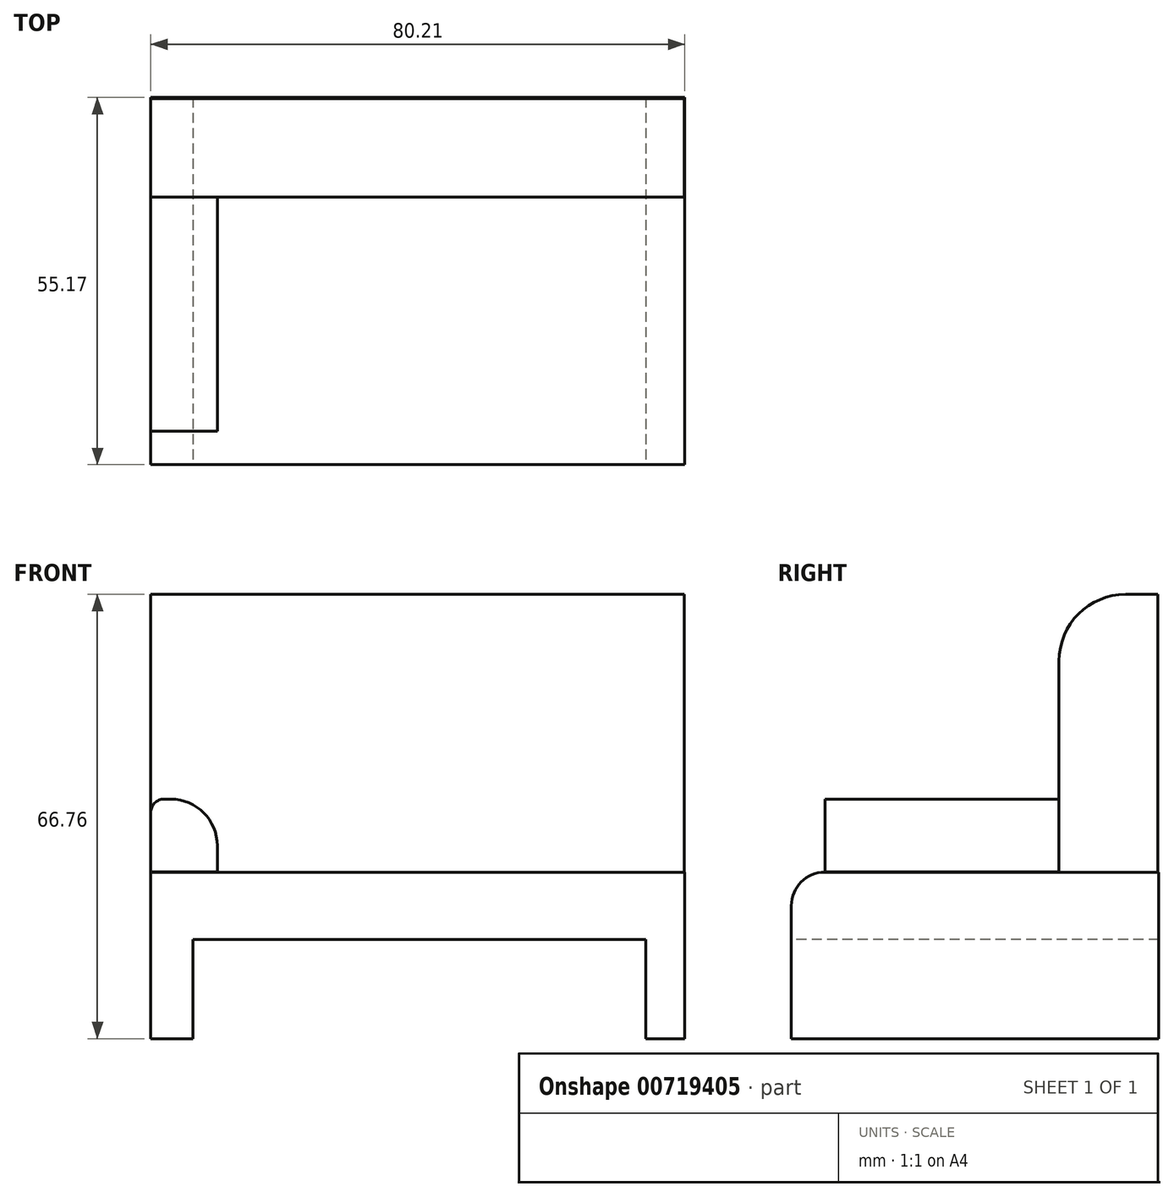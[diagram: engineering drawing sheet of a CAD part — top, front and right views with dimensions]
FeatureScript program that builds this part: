
annotation { "Feature Type Name" : "Feature", "Feature Type Description" : "" }
export const myFeature = defineFeature(function(context is Context, id is Id, definition is map)
    precondition{}
    {
        {
            var Q0;
            Q0=qCreatedBy(makeId("Top.planeOp"),FACE);
            var sketch = newSketch(context, id + "F0", { "sketchPlane" : qUnion([Q0])});
            skLineSegment(sketch, "E0.bottom", {"start": v(0, 0) * mm, "end": v(80.21, 0) * mm});
            skLineSegment(sketch, "E0.top", {"start": v(0, 55.17) * mm, "end": v(80.21, 55.17) * mm});
            skLineSegment(sketch, "E0.left", {"start": v(0, 0) * mm, "end": v(0, 55.17) * mm});
            skLineSegment(sketch, "E0.right", {"start": v(80.21, 0) * mm, "end": v(80.21, 55.17) * mm});
            skSolve(sketch);
        }
        {
            var Q0;
            Q0=makeQuery(id+"F0.imprint","IMPRINT",FACE,{"disambiguationData":[TD([[makeQuery(id+"F0.imprint","IMPRINT",EDGE,{"derivedFrom":sQuery(id+"F0.wireOp",EDGE,"E0.bottom")}),1.0]])]});
            extrude(context, id + "F1", {"entities" : qUnion([Q0]), "depth" : 25 * mm, "offsetDistance" : 25 * mm});
        }
        {
            var Q0;
            Q0=qCreatedBy(makeId("Front.planeOp"),FACE);
            cPlane(context, id + "F2", {"entities" : qUnion([Q0]), "cplaneType" : CPlaneType.OFFSET, "offset" : 55 * mm, "oppositeDirection" : true, "width" : 150 * mm, "height" : 150 * mm});
        }
        {
            var Q0;
            Q0=qCreatedBy(id+"F2.planeOp",FACE);
            var sketch = newSketch(context, id + "F3", { "sketchPlane" : qUnion([Q0])});
            skLineSegment(sketch, "E1.bottom", {"start": v(80.1, 0) * mm, "end": v(0, 0) * mm});
            skLineSegment(sketch, "E1.top", {"start": v(80.1, 66.76) * mm, "end": v(0, 66.76) * mm});
            skLineSegment(sketch, "E1.left", {"start": v(80.1, 0) * mm, "end": v(80.1, 66.76) * mm});
            skLineSegment(sketch, "E1.right", {"start": v(0, 0) * mm, "end": v(0, 66.76) * mm});
            skSolve(sketch);
        }
        {
            var Q0;
            Q0 = qSketchRegion(id + "F3", true);
            extrude(context, id + "F4", {"entities" : qUnion([Q0]), "operationType" : NewBodyOperationType.ADD, "depth" : 14.8 * mm, "offsetDistance" : 25 * mm});
        }
        {
            var Q0;
            Q0=qCreatedBy(makeId("Right.planeOp"),FACE);
            cPlane(context, id + "F5", {"entities" : qUnion([Q0]), "cplaneType" : CPlaneType.OFFSET, "offset" : 40 * mm, "width" : 150 * mm, "height" : 150 * mm});
        }
        {
            var Q0;
            Q0=qCreatedBy(makeId("Front.planeOp"),FACE);
            var sketch = newSketch(context, id + "F6", { "sketchPlane" : qUnion([Q0])});
            skLineSegment(sketch, "E2.bottom", {"start": v(6.36, 0) * mm, "end": v(74.33, 0) * mm});
            skLineSegment(sketch, "E2.top", {"start": v(6.36, 14.87) * mm, "end": v(74.33, 14.87) * mm});
            skLineSegment(sketch, "E2.left", {"start": v(6.36, 0) * mm, "end": v(6.36, 14.87) * mm});
            skLineSegment(sketch, "E2.right", {"start": v(74.33, 0) * mm, "end": v(74.33, 14.87) * mm});
            skSolve(sketch);
        }
        {
            var Q0;
            Q0 = qSketchRegion(id + "F6", true);
            extrude(context, id + "F7", {"entities" : qUnion([Q0]), "operationType" : NewBodyOperationType.REMOVE, "oppositeDirection" : true, "depth" : 99 * mm, "offsetDistance" : 25 * mm});
        }
        {
            var Q0;
            Q0=makeQuery(id+"F1.opExtrude","CAP_EDGE",EDGE,{"disambiguationData":[OSD([sQuery(id+"F0.wireOp",EDGE,"E0.bottom")])],"isStart":false});
            fillet(context, id + "F8", {"entities" : qUnion([Q0]), "radius" : 5 * mm, "tangentPropagation" : true, "allowEdgeOverflow" : false});
        }
        {
            var Q0;
            Q0=qCreatedBy(makeId("Right.planeOp"),FACE);
            var sketch = newSketch(context, id + "F9", { "sketchPlane" : qUnion([Q0])});
            skLineSegment(sketch, "E3.bottom", {"start": v(40.64, 35.99) * mm, "end": v(5.04, 35.99) * mm});
            skLineSegment(sketch, "E3.top", {"start": v(40.64, 25.03) * mm, "end": v(5.04, 25.03) * mm});
            skLineSegment(sketch, "E3.left", {"start": v(40.64, 35.99) * mm, "end": v(40.64, 25.03) * mm});
            skLineSegment(sketch, "E3.right", {"start": v(5.04, 35.99) * mm, "end": v(5.04, 25.03) * mm});
            skSolve(sketch);
        }
        {
            var Q0;
            Q0 = qSketchRegion(id + "F9", true);
            extrude(context, id + "F10", {"entities" : qUnion([Q0]), "operationType" : NewBodyOperationType.ADD, "depth" : 10 * mm, "offsetDistance" : 25 * mm});
        }
        {
            var Q0;
            Q0=makeQuery(id+"F10.opExtrude","CAP_EDGE",EDGE,{"disambiguationData":[OSD([sQuery(id+"F9.wireOp",EDGE,"E3.bottom")])],"isStart":false});
            var Q1;
            Q1=makeQuery(id+"FO4lgylRjQf8yb6_1.1.F10.opExtrude","CAP_EDGE",EDGE,{"disambiguationData":[OSD([sQuery(id+"F9.wireOp",EDGE,"E3.bottom")])],"isStart":false});
            fillet(context, id + "F11", {"entities" : qUnion([Q0, Q1]), "radius" : 7 * mm, "tangentPropagation" : true, "allowEdgeOverflow" : false});
        }
        {
            var Q0;
            Q0=makeQuery(id+"F10.opExtrude","CAP_EDGE",EDGE,{"disambiguationData":[OSD([sQuery(id+"F9.wireOp",EDGE,"E3.bottom")])],"isStart":true});
            var Q1;
            Q1=makeQuery(id+"FO4lgylRjQf8yb6_1.1.F10.opExtrude","CAP_EDGE",EDGE,{"disambiguationData":[OSD([sQuery(id+"F9.wireOp",EDGE,"E3.bottom")])],"isStart":true});
            fillet(context, id + "F12", {"entities" : qUnion([Q0, Q1]), "radius" : 2 * mm, "tangentPropagation" : true, "allowEdgeOverflow" : false});
        }
        {
            var Q0;
            Q0=makeQuery(id+"F4.opExtrude","CAP_EDGE",EDGE,{"disambiguationData":[OSD([sQuery(id+"F3.wireOp",EDGE,"E1.top")])],"isStart":false});
            fillet(context, id + "F13", {"entities" : qUnion([Q0]), "radius" : 10 * mm, "tangentPropagation" : true, "allowEdgeOverflow" : false});
        }
    });
